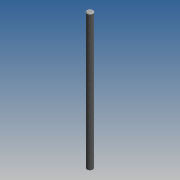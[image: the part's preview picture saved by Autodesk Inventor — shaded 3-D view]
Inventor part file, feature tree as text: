
AUTODESK INVENTOR PART (.ipt)
format: ipt  version: 2019 (Build 230136000, 136)  size: 193,024 bytes
history: native  units: mm
features: extrude x1, chamfer x1, thread x1, sketch x1
ambient origin geometry x8: Origin, YZ Plane, XZ Plane, XY Plane, X Axis, Y Axis, Z Axis, Center Point
bodies: Solid1 (feature_tree)
feature tree (4):
  extrude  "Extrusion1"  Depth=70.0mm TaperAngle=0.0deg
  chamfer  "Chamfer1"  Distance=0.3mm Angle=45.0deg
  thread  "Thread1"  [1 undecoded]
  sketch  "Sketch1"  dims[d0=3.0mm d1=70.0mm d2=0.0mm d3=0.3mm d4=2.0mm d5=45.0deg d6=10.0mm d7=0.0mm]
note: 1 required parameter value undecoded (feature->parameter linkage not recoverable at this tier; creation-order binding heuristic only, values carry confidence <= 0.55)
